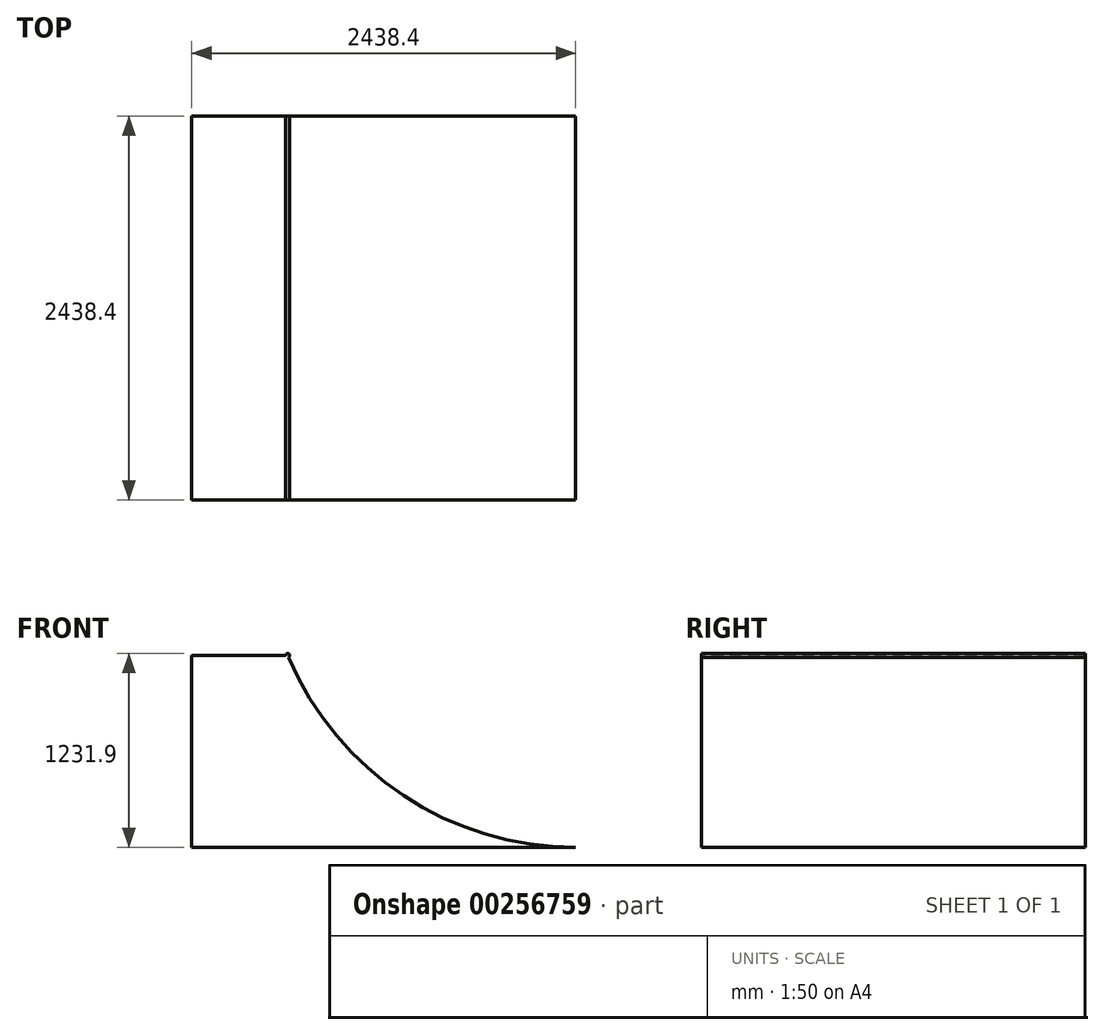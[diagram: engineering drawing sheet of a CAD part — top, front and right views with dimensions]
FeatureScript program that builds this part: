
annotation { "Feature Type Name" : "Feature", "Feature Type Description" : "" }
export const myFeature = defineFeature(function(context is Context, id is Id, definition is map)
    precondition{}
    {
        {
            var Q0;
            Q0=qCreatedBy(makeId("Front.planeOp"),FACE);
            var sketch = newSketch(context, id + "F0", { "sketchPlane" : qUnion([Q0])});
            skLineSegment(sketch, "E0.bottom", {"start": v(0, 0) * mm, "end": v(-2438.4, 0) * mm});
            skLineSegment(sketch, "E0.top", {"start": v(0, 1219.2) * mm, "end": v(-2438.4, 1219.2) * mm});
            skLineSegment(sketch, "E0.left", {"start": v(0, 0) * mm, "end": v(0, 1219.2) * mm});
            skLineSegment(sketch, "E0.right", {"start": v(-2438.4, 0) * mm, "end": v(-2438.4, 1219.2) * mm});
            skArc(sketch, "E1", {"start": v(-1828.8, 1219.2) * mm, "mid": v(-1098.97, 332.74) * mm, "end": v(0, 0) * mm});
            skCircle(sketch, "E2", {"center": v(-1828.8, 1219.2) * mm, "radius": 12.7 * mm});
            skSolve(sketch);
        }
        {
            var Q0;
            {var subQ1=sQuery(id+"F0.wireOp",EDGE,"E0.bottom");Q0=makeQuery(id+"F0.imprint","IMPRINT",FACE,{"disambiguationData":[TD([[makeQuery(id+"F0.imprint","IMPRINT",EDGE,{"derivedFrom":subQ1}),-1.0]])]});}
            var Q1;
            {var subQ0=sQuery(id+"F0.wireOp",EDGE,"E0.top");var subQ1=makeQuery(id+"F0.imprint","INTERSECT",VERTEX,{"derivedFrom":[subQ0,sQuery(id+"F0.wireOp",EDGE,"E1")]});Q1=makeQuery(id+"F0.imprint","IMPRINT",FACE,{"disambiguationData":[TD([[makeQuery(id+"F0.imprint","IMPRINT",EDGE,{"disambiguationData":[TD([[subQ1,1.0]])],"derivedFrom":subQ0}),-1.0]])]});}
            var Q2;
            {var subQ0=sQuery(id+"F0.wireOp",EDGE,"E1");var subQ1=sQuery(id+"F0.wireOp",EDGE,"E0.top");var subQ2=makeQuery(id+"F0.imprint","INTERSECT",VERTEX,{"derivedFrom":[subQ1,subQ0]});Q2=makeQuery(id+"F0.imprint","IMPRINT",FACE,{"disambiguationData":[TD([[makeQuery(id+"F0.imprint","IMPRINT",EDGE,{"disambiguationData":[TD([[subQ2,1.0]])],"derivedFrom":subQ1}),1.0]])]});}
            var Q3;
            {var subQ0=sQuery(id+"F0.wireOp",EDGE,"E1");var subQ1=sQuery(id+"F0.wireOp",EDGE,"E0.top");var subQ2=makeQuery(id+"F0.imprint","INTERSECT",VERTEX,{"derivedFrom":[subQ1,subQ0]});Q3=makeQuery(id+"F0.imprint","IMPRINT",FACE,{"disambiguationData":[TD([[makeQuery(id+"F0.imprint","IMPRINT",EDGE,{"disambiguationData":[TD([[subQ2,-1.0]])],"derivedFrom":subQ1}),1.0]])]});}
            extrude(context, id + "F1", {"entities" : qUnion([Q0, Q1, Q2, Q3]), "oppositeDirection" : true, "depth" : 2438.4 * mm, "symmetric" : true});
        }
    });
